FCSTD DOCUMENT  (FreeCAD 0.21R33668 +26 (Git))
Label: small-baker-spatula
License: All rights reserved
LicenseURL: https://en.wikipedia.org/wiki/All_rights_reserved
objects: TechDraw::DrawViewDimension×7, App::Link×5, TechDraw::DrawViewBalloon×3, TechDraw::DrawProjGroupItem×2, TechDraw::DrawLeaderLine×2, TechDraw::DrawRichAnno×2, App::Part×1, TechDraw::DrawSVGTemplate×1, TechDraw::DrawProjGroup×1, Spreadsheet::Sheet×1, TechDraw::DrawViewImage×1, TechDraw::DrawViewSpreadsheet×1, TechDraw::DrawPage×1
note: 13 computed .brp shape members not serialized (recipe doc carries the construction recipe); baked Part::Feature solids carry a one-line shape summary decoded from their .brp
EXTERNAL_REF file=spatula.FCStd obj=Part
EXTERNAL_REF file=handle.FCStd obj=Part001
EXTERNAL_REF file=dowel.FCStd obj=Part002

FEATURE [App::Link] Link  label="spatula"
  LinkedObject = -> <external spatula.FCStd>#Part
FEATURE [App::Link] Link001  label="handle-01"
  LinkPlacement = pos=(0,-30,2) rot=(0,0,1;0rad)
  LinkedObject = -> <external handle.FCStd>#Part001
  Placement = pos=(0,-30,2) rot=(0,0,1;0rad)
FEATURE [App::Link] Link002  label="handle-02"
  LinkPlacement = pos=(0,-30,0) rot=(0,1,0;3.14159rad)
  LinkedObject = -> <external handle.FCStd>#Part001
  Placement = pos=(0,-30,0) rot=(0,1,0;3.14159rad)
FEATURE [App::Link] Link003  label="dowel-01"
  LinkPlacement = pos=(0,-30,1) rot=(0,0,1;0rad)
  LinkedObject = -> <external dowel.FCStd>#Part002
  Placement = pos=(0,-30,1) rot=(0,0,1;0rad)
FEATURE [App::Link] Link004  label="dowel-02"
  LinkPlacement = pos=(-100,-30,1) rot=(0,0,1;0rad)
  LinkedObject = -> <external dowel.FCStd>#Part002
  Placement = pos=(-100,-30,1) rot=(0,0,1;0rad)
FEATURE [App::Part] Part
  Group = -> [Link,Link001,Link002,Link003,Link004]
  Origin = -> Origin
FEATURE [TechDraw::DrawSVGTemplate] Template
  Height = 210
  Orientation = 1
  Template = <userpath>/AppData/Local/Programs/FreeCAD 0.21/data/Mod/TechDraw/Templates/A4_Landscape_ISO7200_Core.svg
  Width = 297
FEATURE [TechDraw::DrawProjGroupItem] ProjItem
  CoarseView = false
  Direction = (0,0,1)
  Focus = 100
  HardHidden = false
  IsoCount = 0
  IsoHidden = false
  IsoVisible = false
  LockPosition = true
  Perspective = false
  Rotation = 0
  RotationVector = (-1,0,0)
  Scale = 0.5
  ScaleType = 2
  ScrubCount = 0
  SeamHidden = false
  SeamVisible = false
  SmoothHidden = false
  SmoothVisible = true
  Source = -> [Part]
  Type = 0
  X = 0
  XDirection = (-1,0,0)
  Y = 0
FEATURE [TechDraw::DrawProjGroupItem] ProjItem001
  CoarseView = true
  Direction = (1,0,1e-16)
  Focus = 100
  HardHidden = false
  IsoCount = 0
  IsoHidden = false
  IsoVisible = false
  LockPosition = false
  Perspective = false
  Rotation = 0
  RotationVector = (1,0,0)
  ScaleType = 2
  ScrubCount = 0
  SeamHidden = false
  SeamVisible = false
  SmoothHidden = false
  SmoothVisible = false
  Source = -> [Part]
  Type = 1
  X = 95.5
  XDirection = (-1e-16,0,1)
  Y = 0
FEATURE [TechDraw::DrawProjGroup] ProjGroup
  Anchor = -> ProjItem
  AutoDistribute = true
  LockPosition = false
  ProjectionType = 0
  Rotation = 0
  Scale = 0.5
  ScaleType = 2
  Source = -> [Part]
  Views = -> [ProjItem,ProjItem001]
  X = 91.6312
  Y = 136.54
  spacingX = 50
  spacingY = 15
FEATURE [Spreadsheet::Sheet] Spreadsheet  label="Nomenclature"
  cells = A1='Id; B1='Nom; C1='Part; D1='Quantité; E1='Matière; F1='Spécifications; G1='Notes; A2=1; B2='Spatule; C2='spatula; D2=1; E2='Inox (316L); F2='160x100x2; A3=2; B3='Poignée; C3='handle; D3=2; E3='Bois (Chêne); F3='160x40x10; A4=3; B4='Cheville; C4='dowel; D4=2; E4='Bois (Hêtre); F4='⌀10x22
FEATURE [TechDraw::DrawViewImage] Image
  Height = 100
  ImageFile = <userpath>/OneDrive - TEN/devOps-projects/low-tech-hardware/small-baker-spatula/small-baker-spatula.jpg
  LockPosition = false
  Rotation = 0
  Scale = 0.3
  ScaleType = 2
  Width = 100
  X = 53.8285
  Y = 45.8534
FEATURE [TechDraw::DrawViewSpreadsheet] Sheet
  CellEnd = G4
  CellStart = A1
  Font = osifont
  LineWidth = 0.35
  LockPosition = false
  Rotation = 0
  ScaleType = 2
  Source = -> Spreadsheet
  Symbol = <blob: 6410 chars omitted>
  TextSize = 12
  X = 214.573
  Y = 60.284
FEATURE [TechDraw::DrawViewDimension] Dimension003
  AngleOverride = false
  Arbitrary = false
  ArbitraryTolerances = false
  EqualTolerance = true
  ExtensionAngle = 0
  FormatSpec = 2x⌀%.2w
  FormatSpecOverTolerance = %+.2w
  FormatSpecUnderTolerance = %+.2w
  Inverted = false
  LineAngle = 0
  LockPosition = false
  MeasureType = 1
  OverTolerance = 0
  References2D = -> [ProjItem]
  Rotation = 0
  ScaleType = 0
  TheoreticalExact = false
  Type = 5
  UnderTolerance = 0
  X = -65.7159
  Y = 43.4736
FEATURE [TechDraw::DrawViewDimension] Dimension004
  AngleOverride = false
  Arbitrary = false
  ArbitraryTolerances = false
  EqualTolerance = true
  ExtensionAngle = 0
  FormatSpec = %.2w
  FormatSpecOverTolerance = %+.2w
  FormatSpecUnderTolerance = %+.2w
  Inverted = false
  LineAngle = 0
  LockPosition = false
  MeasureType = 1
  OverTolerance = 0
  References2D = -> [ProjItem]
  Rotation = 0
  ScaleType = 0
  TheoreticalExact = false
  Type = 1
  UnderTolerance = 0
  X = -0.655162
  Y = 39.1981
FEATURE [TechDraw::DrawViewDimension] Dimension005
  AngleOverride = false
  Arbitrary = false
  ArbitraryTolerances = false
  EqualTolerance = true
  ExtensionAngle = 0
  FormatSpec = %.2w
  FormatSpecOverTolerance = %+.2w
  FormatSpecUnderTolerance = %+.2w
  Inverted = false
  LineAngle = 0
  LockPosition = false
  MeasureType = 1
  OverTolerance = 0
  References2D = -> [ProjItem]
  Rotation = 0
  ScaleType = 0
  TheoreticalExact = false
  Type = 1
  UnderTolerance = 0
  X = -1.14654
  Y = 51.5773
FEATURE [TechDraw::DrawViewDimension] Dimension006
  AngleOverride = false
  Arbitrary = false
  ArbitraryTolerances = false
  EqualTolerance = true
  ExtensionAngle = 0
  FormatSpec = %.2w
  FormatSpecOverTolerance = %+.2w
  FormatSpecUnderTolerance = %+.2w
  Inverted = false
  LineAngle = 0
  LockPosition = false
  MeasureType = 1
  OverTolerance = 0
  References2D = -> [ProjItem001]
  Rotation = 0
  ScaleType = 0
  TheoreticalExact = false
  Type = 2
  UnderTolerance = 0
  X = -16.8272
  Y = 17.6947
FEATURE [TechDraw::DrawViewDimension] Dimension
  AngleOverride = false
  Arbitrary = false
  ArbitraryTolerances = false
  EqualTolerance = true
  ExtensionAngle = 0
  FormatSpec = %.2w
  FormatSpecOverTolerance = %+.2w
  FormatSpecUnderTolerance = %+.2w
  Inverted = false
  LineAngle = 0
  LockPosition = false
  MeasureType = 1
  OverTolerance = 0
  References2D = -> [ProjItem]
  Rotation = 0
  ScaleType = 0
  TheoreticalExact = false
  Type = 2
  UnderTolerance = 0
  X = -58.7969
  Y = 3.08285
FEATURE [TechDraw::DrawViewDimension] Dimension007
  AngleOverride = false
  Arbitrary = false
  ArbitraryTolerances = false
  EqualTolerance = true
  ExtensionAngle = 0
  FormatSpec = %.2w
  FormatSpecOverTolerance = %+.2w
  FormatSpecUnderTolerance = %+.2w
  Inverted = false
  LineAngle = 0
  LockPosition = false
  MeasureType = 1
  OverTolerance = 0
  References2D = -> [ProjItem001]
  Rotation = 0
  ScaleType = 0
  TheoreticalExact = false
  Type = 1
  UnderTolerance = 0
  X = -14.7874
  Y = 38.8445
FEATURE [TechDraw::DrawViewDimension] Dimension008
  AngleOverride = false
  Arbitrary = false
  ArbitraryTolerances = false
  EqualTolerance = true
  ExtensionAngle = 0
  FormatSpec = %.2w
  FormatSpecOverTolerance = %+.2w
  FormatSpecUnderTolerance = %+.2w
  Inverted = false
  LineAngle = 0
  LockPosition = false
  MeasureType = 1
  OverTolerance = 0
  References2D = -> [ProjItem001]
  Rotation = 0
  ScaleType = 0
  TheoreticalExact = false
  Type = 1
  UnderTolerance = 0
  X = -15.0889
  Y = -23.5222
FEATURE [TechDraw::DrawViewBalloon] Balloon
  BubbleShape = 0
  EndType = 0
  EndTypeScale = 1
  KinkLength = 5
  LockPosition = false
  OriginX = 5
  OriginY = 50
  Rotation = 0
  ScaleType = 0
  ShapeScale = 1
  SourceView = -> ProjItem001
  Text = 2
  TextWrapLen = -1
  X = 53.6253
  Y = 74.9057
FEATURE [TechDraw::DrawViewBalloon] Balloon001
  BubbleShape = 0
  EndType = 0
  EndTypeScale = 1
  KinkLength = 5
  LockPosition = false
  OriginX = 1
  OriginY = 2
  Rotation = 0
  ScaleType = 0
  ShapeScale = 1
  SourceView = -> ProjItem001
  Text = 1
  TextWrapLen = -1
  X = 51.1078
  Y = -19.2084
FEATURE [TechDraw::DrawViewBalloon] Balloon002
  BubbleShape = 0
  EndType = 0
  EndTypeScale = 1
  KinkLength = 5
  LockPosition = false
  OriginX = 55
  OriginY = 30
  Rotation = 0
  ScaleType = 0
  ShapeScale = 1
  SourceView = -> ProjItem
  Text = 3
  TextWrapLen = -1
  X = 114.498
  Y = 20.7132
FEATURE [TechDraw::DrawLeaderLine] LeaderLine
  AutoHorizontal = true
  EndSymbol = 7
  LeaderParent = -> ProjItem001
  LockPosition = true
  Rotation = 0
  Scalable = false
  ScaleType = 0
  StartSymbol = 0
  WayPoints = (3) [(0,0,0),(156.382,-64.7755,0),(315.508,-64.7755,0)]
  X = 10.2947
  Y = 11.3978
FEATURE [TechDraw::DrawRichAnno] RichTextAnnotation
  AnnoParent = -> LeaderLine
  AnnoText = <!DOCTYPE HTML PUBLIC "-//W3C//DTD HTML 4.0//EN" "http://www.w3.org/TR/REC-html40/strict.dtd">\n<html><head><meta name="qrichtext" content="1" /><style type="text/css">\np, li { white-space: pre-wrap; }\n</style></head><body style=" font-family:'osifont'; font-size:8.25pt; font-weight:400; font-style:normal;">\n<p style=" margin-top:0px; margin-bottom:0px; margin-left:0px; margin-right:0px; -qt-block-indent:0; text-indent:0px;"><span style=" font-family:'MS Shell Dlg 2'; font-size:8pt;">Les arêtes extérieures des poignées </span></p>\n<p style=" margin-top:0px; margin-bottom:0px; margin-left:0px; margin-right:0px; -qt-block-indent:0; text-indent:0px;"><span style=" font-family:'MS Shell Dlg 2'; font-size:8pt;">sont légèrement chanfreinées</span></p></body></html>
  LockPosition = false
  MaxWidth = -1
  Rotation = 0
  ScaleType = 0
  ShowFrame = false
  X = 64.133
  Y = 6.5045
FEATURE [TechDraw::DrawLeaderLine] LeaderLine001
  AutoHorizontal = true
  EndSymbol = 7
  LeaderParent = -> ProjItem
  LockPosition = true
  Rotation = 0
  Scalable = false
  ScaleType = 0
  StartSymbol = 0
  WayPoints = (3) [(0,0,0),(-209.119,209.119,0),(-380.905,209.119,0)]
  X = 33.3251
  Y = -50.1438
FEATURE [TechDraw::DrawRichAnno] RichTextAnnotation001
  AnnoParent = -> LeaderLine001
  AnnoText = <!DOCTYPE HTML PUBLIC "-//W3C//DTD HTML 4.0//EN" "http://www.w3.org/TR/REC-html40/strict.dtd">\n<html><head><meta name="qrichtext" content="1" /><style type="text/css">\np, li { white-space: pre-wrap; }\n</style></head><body style=" font-family:'MS Shell Dlg 2'; font-size:8.25pt; font-weight:400; font-style:normal;">\n<p style=" margin-top:0px; margin-bottom:0px; margin-left:0px; margin-right:0px; -qt-block-indent:0; text-indent:0px;"><span style=" font-family:'osifont'; font-size:8pt;">La géométrie de l'émouture doit</span></p>\n<p style=" margin-top:0px; margin-bottom:0px; margin-left:0px; margin-right:0px; -qt-block-indent:0; text-indent:0px;"><span style=" font-family:'osifont'; font-size:8pt;">être adaptée au besoin</span></p></body></html>
  LockPosition = false
  MaxWidth = -1
  Rotation = 0
  ScaleType = 0
  ShowFrame = false
  X = -64.6775
  Y = -19.7871
FEATURE [TechDraw::DrawPage] Page  label="Drawing"
  KeepUpdated = true
  NextBalloonIndex = 10
  ProjectionType = 0
  Template = -> Template
  Views = -> [ProjGroup,Image,Sheet,Dimension003,Dimension004,Dimension005,Dimension006,Dimension,Dimension007,Dimension008,Balloon,Balloon001,Balloon002,LeaderLine,RichTextAnnotation,LeaderLine001,RichTextAnnotation001]

RESOLVED EXTERNAL PARTS (link-assembly join: the EXTERNAL_REF files above that resolve inside this repo's crawl, each included once):
---- part dowel.FCStd = doc fcstd_9c20e7385713 ----
FCSTD DOCUMENT  (FreeCAD 0.21R33668 +26 (Git))
Label: dowel
License: All rights reserved
LicenseURL: https://en.wikipedia.org/wiki/All_rights_reserved
objects: Sketcher::SketchObject×1, PartDesign::Pad×1, PartDesign::Body×1, App::Part×1
note: 4 computed .brp shape members not serialized (recipe doc carries the construction recipe); baked Part::Feature solids carry a one-line shape summary decoded from their .brp

FEATURE [Sketcher::SketchObject] Sketch003
  FullyConstrained = true
  MapMode = 5
  Support = -> [XY_Plane005]
  sketch-geometry (1):
    g0: Circle CenterX=50 CenterY=0 CenterZ=0 NormalX=0 NormalY=0 NormalZ=1 AngleXU=0 Radius=5
  constraints (3):
    c: PointOnObject(g0,g-1)
    c: Diameter(g0) = 10
    c: DistanceX(g0) = 50
FEATURE [PartDesign::Pad] Pad002
  Direction = (0,0,1)
  Length = 22
  Length2 = 10
  Midplane = true
  Profile = -> Sketch003
  ReferenceAxis = -> Sketch003 [N_Axis]
  Type = 0
FEATURE [PartDesign::Body] Body002  label="Body"
  Group = -> [Sketch003,Pad002]
  Origin = -> Origin005
  Tip = -> Pad002
FEATURE [App::Part] Part002  label="Part"
  Group = -> [Body002]
  Origin = -> Origin004
---- part handle.FCStd = doc fcstd_d6daa0114656 ----
FCSTD DOCUMENT  (FreeCAD 0.21R33668 +26 (Git))
Label: handle
License: All rights reserved
LicenseURL: https://en.wikipedia.org/wiki/All_rights_reserved
objects: Sketcher::SketchObject×1, PartDesign::Pad×1, PartDesign::Chamfer×1, PartDesign::Body×1, App::Part×1
note: 6 computed .brp shape members not serialized (recipe doc carries the construction recipe); baked Part::Feature solids carry a one-line shape summary decoded from their .brp

FEATURE [Sketcher::SketchObject] Sketch002
  FullyConstrained = true
  MapMode = 5
  Support = -> [XY_Plane003]
  sketch-geometry (7):
    g0: LineSegment StartX=-80 StartY=20 StartZ=0 EndX=-80 EndY=-20 EndZ=0
    g1: LineSegment StartX=-80 StartY=-20 StartZ=0 EndX=80 EndY=-20 EndZ=0
    g2: LineSegment StartX=80 StartY=-20 StartZ=0 EndX=80 EndY=20 EndZ=0
    g3: LineSegment StartX=80 StartY=20 StartZ=0 EndX=-80 EndY=20 EndZ=0
    g4: GeomPoint X=0 Y=0 Z=0
    g5: Circle CenterX=-50 CenterY=0 CenterZ=0 NormalX=0 NormalY=0 NormalZ=1 AngleXU=0 Radius=5
    g6: Circle CenterX=50 CenterY=0 CenterZ=0 NormalX=0 NormalY=0 NormalZ=1 AngleXU=0 Radius=5
  constraints (17):
    c: Coincident(g0,g1)
    c: Coincident(g1,g2)
    c: Coincident(g2,g3)
    c: Coincident(g3,g0)
    c: Horizontal(g1)
    c: Horizontal(g3)
    c: Vertical(g0)
    c: Vertical(g2)
    c: Symmetric(g1,g0,g4)
    c: Coincident(g4,g-1)
    c: DistanceX(g3,g3) = 160
    c: DistanceY(g2,g2) = 40
    c: PointOnObject(g5,g-1)
    c: Diameter(g5) = 10
    c: Diameter(g6) = 10
    c: Symmetric(g5,g6,g-2)
    c: DistanceX(g5,g6) = 100
FEATURE [PartDesign::Pad] Pad001
  Direction = (0,0,1)
  Length = 10
  Length2 = 10
  Profile = -> Sketch002
  ReferenceAxis = -> Sketch002 [N_Axis]
  Type = 0
FEATURE [PartDesign::Chamfer] Chamfer001
  Angle = 45
  Base = -> Pad001 [Edge4,Edge12,Edge10,Edge7]
  BaseFeature = -> Pad001
  ChamferType = 0
  FlipDirection = false
  Size = 2
  Size2 = 1
  SupportTransform = false
  UseAllEdges = false
FEATURE [PartDesign::Body] Body001  label="Body"
  Group = -> [Sketch002,Pad001,Chamfer001]
  Origin = -> Origin003
  Tip = -> Chamfer001
FEATURE [App::Part] Part001  label="Part"
  Group = -> [Body001]
  Origin = -> Origin002
---- part spatula.FCStd = doc fcstd_915341de50db ----
FCSTD DOCUMENT  (FreeCAD 0.21R33668 +26 (Git))
Label: spatula
License: All rights reserved
LicenseURL: https://en.wikipedia.org/wiki/All_rights_reserved
objects: Sketcher::SketchObject×2, PartDesign::Pad×1, PartDesign::Chamfer×1, PartDesign::Pocket×1, PartDesign::Body×1, App::Part×1
note: 9 computed .brp shape members not serialized (recipe doc carries the construction recipe); baked Part::Feature solids carry a one-line shape summary decoded from their .brp

FEATURE [Sketcher::SketchObject] Sketch
  FullyConstrained = true
  MapMode = 5
  Support = -> [XY_Plane001]
  sketch-geometry (5):
    g0: LineSegment StartX=80 StartY=-50 StartZ=0 EndX=80 EndY=50 EndZ=0
    g1: LineSegment StartX=80 StartY=50 StartZ=0 EndX=-80 EndY=50 EndZ=0
    g2: LineSegment StartX=-80 StartY=50 StartZ=0 EndX=-80 EndY=-50 EndZ=0
    g3: LineSegment StartX=-80 StartY=-50 StartZ=0 EndX=80 EndY=-50 EndZ=0
    g4: GeomPoint X=0 Y=0 Z=0
  constraints (12):
    c: Coincident(g0,g1)
    c: Coincident(g1,g2)
    c: Coincident(g2,g3)
    c: Coincident(g3,g0)
    c: Horizontal(g1)
    c: Horizontal(g3)
    c: Vertical(g0)
    c: Vertical(g2)
    c: Symmetric(g1,g0,g4)
    c: Coincident(g4,g-1)
    c: DistanceX(g1,g1) = 160
    c: DistanceY(g2,g2) = 100
FEATURE [PartDesign::Pad] Pad
  Direction = (0,0,1)
  Length = 2
  Length2 = 10
  Profile = -> Sketch
  ReferenceAxis = -> Sketch [N_Axis]
  Type = 0
FEATURE [PartDesign::Chamfer] Chamfer
  Angle = 45
  Base = -> Pad [Edge7]
  BaseFeature = -> Pad
  ChamferType = 1
  FlipDirection = false
  Size = 1.5
  Size2 = 4
  SupportTransform = false
  UseAllEdges = false
FEATURE [Sketcher::SketchObject] Sketch001
  ExternalGeometry = -> [Chamfer]
  FullyConstrained = false
  MapMode = 5
  Placement = pos=(0,0,2) rot=(0,0,1;0rad)
  Support = -> [Chamfer]
  sketch-geometry (3):
    g0: LineSegment StartX=-92.5186 StartY=-30 StartZ=0 EndX=57.3629 EndY=-30 EndZ=0
    g1: Circle CenterX=-50 CenterY=-30 CenterZ=0 NormalX=0 NormalY=0 NormalZ=1 AngleXU=0 Radius=5
    g2: Circle CenterX=50 CenterY=-30 CenterZ=0 NormalX=0 NormalY=0 NormalZ=1 AngleXU=0 Radius=5
  constraints (7):
    c: Horizontal(g0)
    c: DistanceY(g-3,g0) = 20
    c: PointOnObject(g1,g0)
    c: Diameter(g1) = 10
    c: Diameter(g2) = 10
    c: Symmetric(g1,g2,g-2)
    c: DistanceX(g1,g2) = 100
FEATURE [PartDesign::Pocket] Pocket
  BaseFeature = -> Chamfer
  Direction = (0,0,-1)
  Length = 5
  Length2 = 5
  Profile = -> Sketch001
  ReferenceAxis = -> Sketch001 [N_Axis]
  Type = 2
FEATURE [PartDesign::Body] Body
  Group = -> [Sketch,Pad,Chamfer,Sketch001,Pocket]
  Origin = -> Origin001
  Tip = -> Pocket
FEATURE [App::Part] Part
  Group = -> [Body]
  Origin = -> Origin
